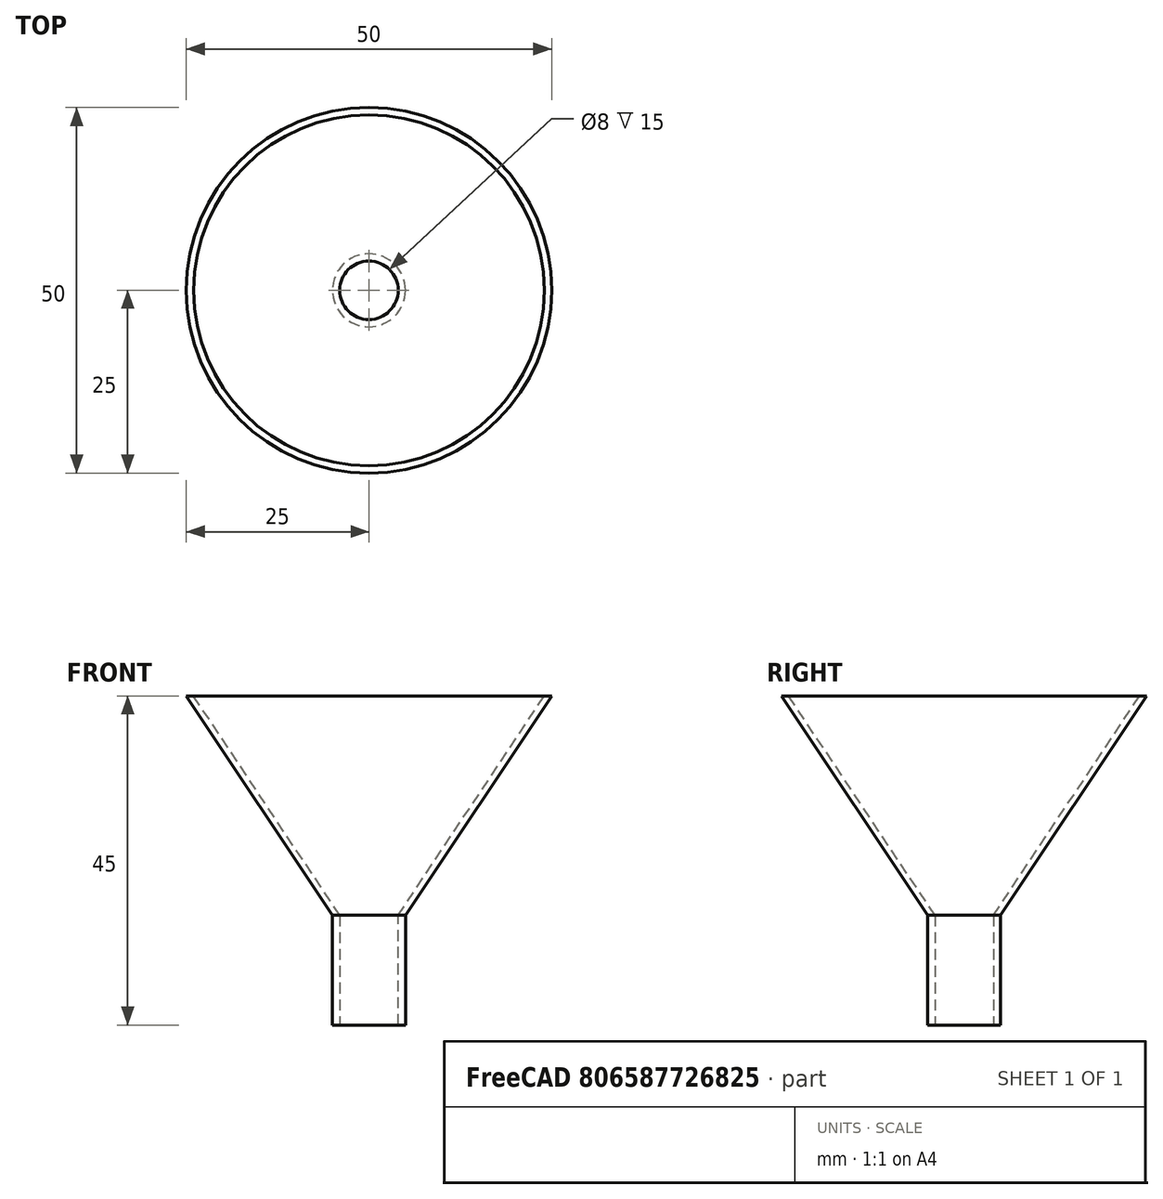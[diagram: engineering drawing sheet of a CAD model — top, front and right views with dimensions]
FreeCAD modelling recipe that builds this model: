
FCSTD DOCUMENT  (FreeCAD 1.0R39319 (Git))
Label: ojt1_t14r03_funnel
License: All rights reserved
LicenseURL: https://en.wikipedia.org/wiki/All_rights_reserved
objects: Part::Cone×2, Part::Cut×2, Part::Cylinder×2, Part::MultiFuse×1
note: 7 computed .brp shape members not serialized (recipe doc carries the construction recipe); baked Part::Feature solids carry a one-line shape summary decoded from their .brp

FEATURE [Part::Cone] Cone
  Angle = 360
  AttacherType = Attacher::AttachEngine3D
  Height = 30
  Radius1 = 5
  Radius2 = 25
FEATURE [Part::Cone] Cone001
  Angle = 360
  AttacherType = Attacher::AttachEngine3D
  Height = 30
  Radius1 = 4
  Radius2 = 24
FEATURE [Part::Cut] Cut
  Base = -> Cone
  Placement = pos=(0,0,15) rot=(0,0,1;0rad)
  Refine = true
  Tool = -> Cone001
FEATURE [Part::Cylinder] Cylinder
  Angle = 360
  AttacherType = Attacher::AttachEngine3D
  FirstAngle = 0
  Height = 15
  Radius = 5
  SecondAngle = 0
FEATURE [Part::Cylinder] Cylinder001
  Angle = 360
  AttacherType = Attacher::AttachEngine3D
  FirstAngle = 0
  Height = 15
  Radius = 4
  SecondAngle = 0
FEATURE [Part::Cut] Cut001
  Base = -> Cylinder
  Refine = true
  Tool = -> Cylinder001
FEATURE [Part::MultiFuse] Fusion
  Refine = true
  Shapes = -> [Cut001,Cut]
